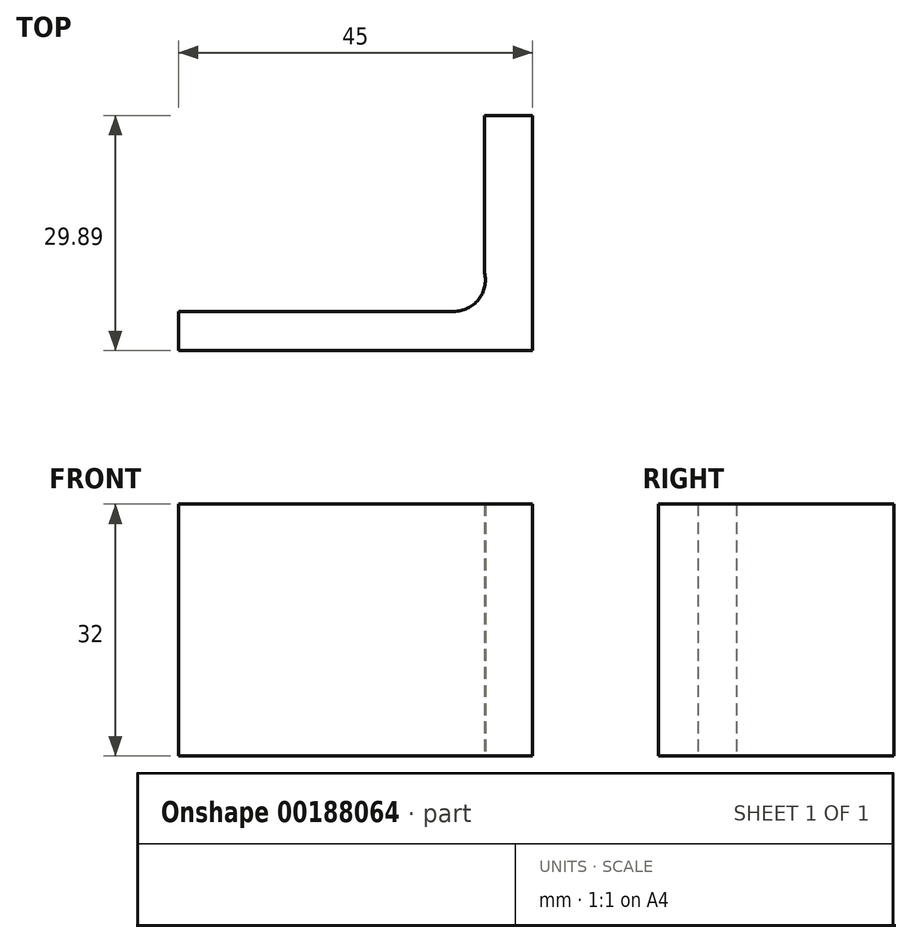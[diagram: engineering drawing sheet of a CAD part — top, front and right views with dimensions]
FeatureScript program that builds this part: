
annotation { "Feature Type Name" : "Feature", "Feature Type Description" : "" }
export const myFeature = defineFeature(function(context is Context, id is Id, definition is map)
    precondition{}
    {
        {
            var Q0;
            Q0=qCreatedBy(makeId("Top.planeOp"),FACE);
            var sketch = newSketch(context, id + "F0", { "sketchPlane" : qUnion([Q0])});
            skLineSegment(sketch, "E0", {"start": v(-50.62, 5.44) * mm, "end": v(-5.62, 5.44) * mm});
            skLineSegment(sketch, "E1", {"start": v(-50.62, 5.44) * mm, "end": v(-50.62, 10.44) * mm});
            skLineSegment(sketch, "E2", {"start": v(-50.62, 10.44) * mm, "end": v(-15.62, 10.44) * mm});
            skLineSegment(sketch, "E3", {"start": v(-5.62, 5.44) * mm, "end": v(-5.62, 10.44) * mm});
            skArc(sketch, "E4", {"start": v(-15.62, 10.44) * mm, "mid": v(-12.5, 11.94) * mm, "end": v(-11.72, 15.33) * mm});
            skLineSegment(sketch, "E5", {"start": v(-11.72, 15.33) * mm, "end": v(-11.72, 35.33) * mm});
            skLineSegment(sketch, "E6", {"start": v(-11.72, 35.33) * mm, "end": v(-5.62, 35.33) * mm});
            skLineSegment(sketch, "E7", {"start": v(-5.62, 35.33) * mm, "end": v(-5.62, 10.44) * mm});
            skSolve(sketch);
        }
        {
            var Q0;
            Q0 = qSketchRegion(id + "F0", true);
            extrude(context, id + "F1", {"entities" : qUnion([Q0]), "depth" : 32 * mm});
        }
    });
